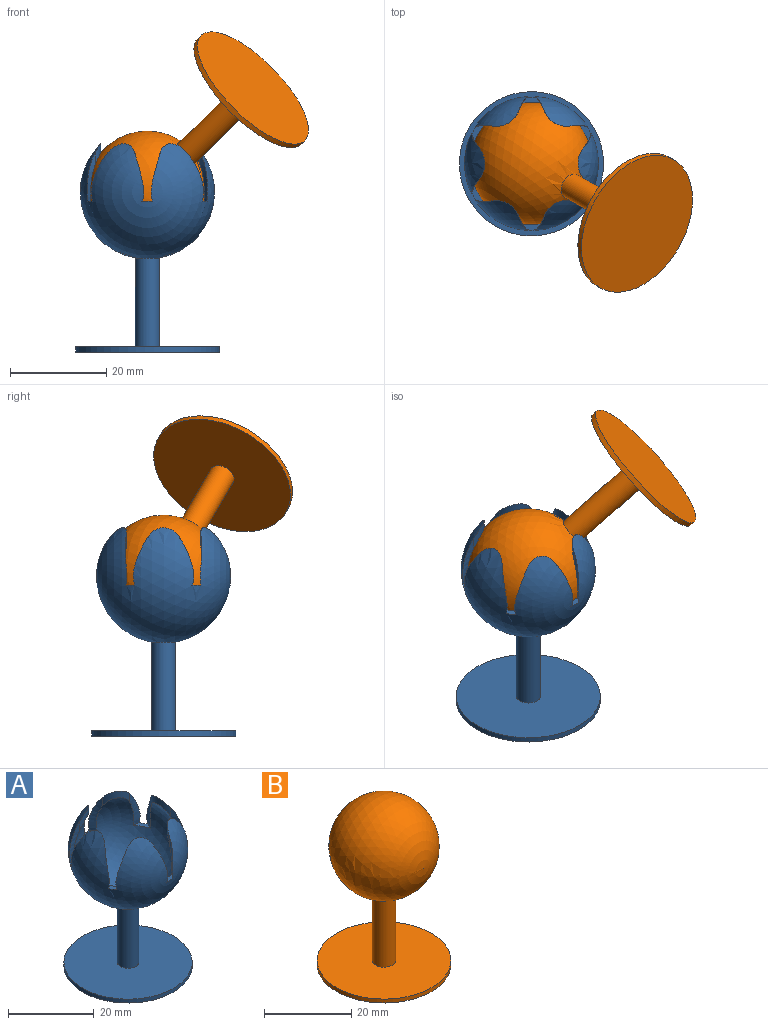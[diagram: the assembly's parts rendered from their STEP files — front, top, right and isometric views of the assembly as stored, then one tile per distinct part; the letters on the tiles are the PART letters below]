
ASSEMBLY  parts=2 mates=1
PART A: 30 faces, bbox 30.5x30.5x47.1 mm
  f0: extruded ~10.07x2.93mm, area 15.8mm2, adj f13,f21,f23,f24
  f1: extruded ~10.07x3.07mm, area 15.8mm2, adj f12,f21,f23,f25
  f2: extruded ~10.07x3.46mm, area 15.8mm2, adj f21,f22,f23,f29
  f3: extruded ~10.07x2.93mm, area 15.8mm2, adj f16,f21,f23,f26
  f4: extruded ~10.07x3.07mm, area 15.8mm2, adj f15,f21,f23,f28
  f5: extruded ~10.07x3.46mm, area 15.8mm2, adj f14,f21,f23,f27
  f6: extruded ~10.07x2.93mm, area 15.8mm2, adj f13,f21,f23,f27
  f7: extruded ~10.07x3.46mm, area 15.8mm2, adj f12,f21,f23,f24
  f8: extruded ~10.07x3.07mm, area 15.8mm2, adj f21,f22,f23,f25
  f9: extruded ~10.07x2.93mm, area 15.8mm2, adj f16,f21,f23,f29
  f10: extruded ~10.07x3.46mm, area 15.8mm2, adj f15,f21,f23,f26
  f11: extruded ~10.07x3.07mm, area 15.8mm2, adj f14,f21,f23,f28
  f12: plane 3.66x2.84mm, normal (0,0,1), area 4.1mm2, adj f1,f7,f21,f23
  f13: plane 4.61x1.95mm, normal (0,0,1), area 4.1mm2, adj f0,f6,f21,f23
  f14: plane 3.66x2.84mm, normal (0,0,1), area 4.1mm2, adj f5,f11,f21,f23
  f15: plane 3.66x2.84mm, normal (0,0,1), area 4.1mm2, adj f4,f10,f21,f23
  f16: plane 4.61x1.95mm, normal (0,0,1), area 4.1mm2, adj f3,f9,f21,f23
  f17: cylinder r=15mm len=30mm, axis (0,0,-1), area 103.7mm2, adj f18,f19
  f18: plane 30x30mm, normal (0,0,1), area 687.2mm2, adj f17,f20
  f19: plane 30x30mm, normal (0,0,-1), area 706.9mm2, adj f17
  f20: cylinder r=2.5mm len=18.45mm, axis (0,0,-1), area 289.8mm2, adj f18,f21
  f21: sphere r=13.97mm, area 1804.4mm2, adj f0,f1,f2,f3,f4,f5,f6,f7
  f22: plane 3.66x2.84mm, normal (0,0,1), area 4.1mm2, adj f2,f8,f21,f23
  f23: sphere r=12.7mm, area 1346.5mm2, adj f0,f1,f2,f3,f4,f5,f6,f7
  f24: cylinder r=5mm len=5.57mm, axis (0,0,1), area 14.2mm2, adj f0,f7,f21,f23
  f25: cylinder r=5mm len=6.43mm, axis (0,0,1), area 14.2mm2, adj f1,f8,f21,f23
  f26: cylinder r=5mm len=5.57mm, axis (0,0,1), area 14.2mm2, adj f3,f10,f21,f23
  f27: cylinder r=5mm len=5.57mm, axis (0,0,1), area 14.2mm2, adj f5,f6,f21,f23
  f28: cylinder r=5mm len=6.43mm, axis (0,0,1), area 14.2mm2, adj f4,f11,f21,f23
  f29: cylinder r=5mm len=5.57mm, axis (0,0,1), area 14.2mm2, adj f2,f9,f21,f23
PART B: 7 faces, bbox 30.8x30.8x46 mm
  f0: cylinder r=15.38mm len=30.76mm, axis (0,0,-1), area 106.3mm2, adj f1,f2
  f1: plane 30.76x30.76mm, normal (0,0,1), area 720.5mm2, adj f0,f3
  f2: plane 30.76x30.76mm, normal (0,0,-1), area 743.2mm2, adj f0
  f3: cylinder r=2.69mm len=19.79mm, axis (0,0,-1), area 334.3mm2, adj f1,f4
  f4: sphere r=12.7mm, area 2003.9mm2, adj f3
  f5: sphere r=2.69mm, area 45.4mm2, adj f6
  f6: plane 5.38x5.38mm, normal (0,0,1), area 22.7mm2, adj f5
PLACE A rot(axis=(0,-1,0),0deg) t=(20.42,25.48,-10.23)mm fixed
PLACE B rot(axis=(-0.33,-0.94,-0.08),131.4deg) t=(42.37,12.9,44.71)mm
MATE ball A.f20 <-> B.f3  axis (0,0,1) through (20.42,25.48,23.07)mm
